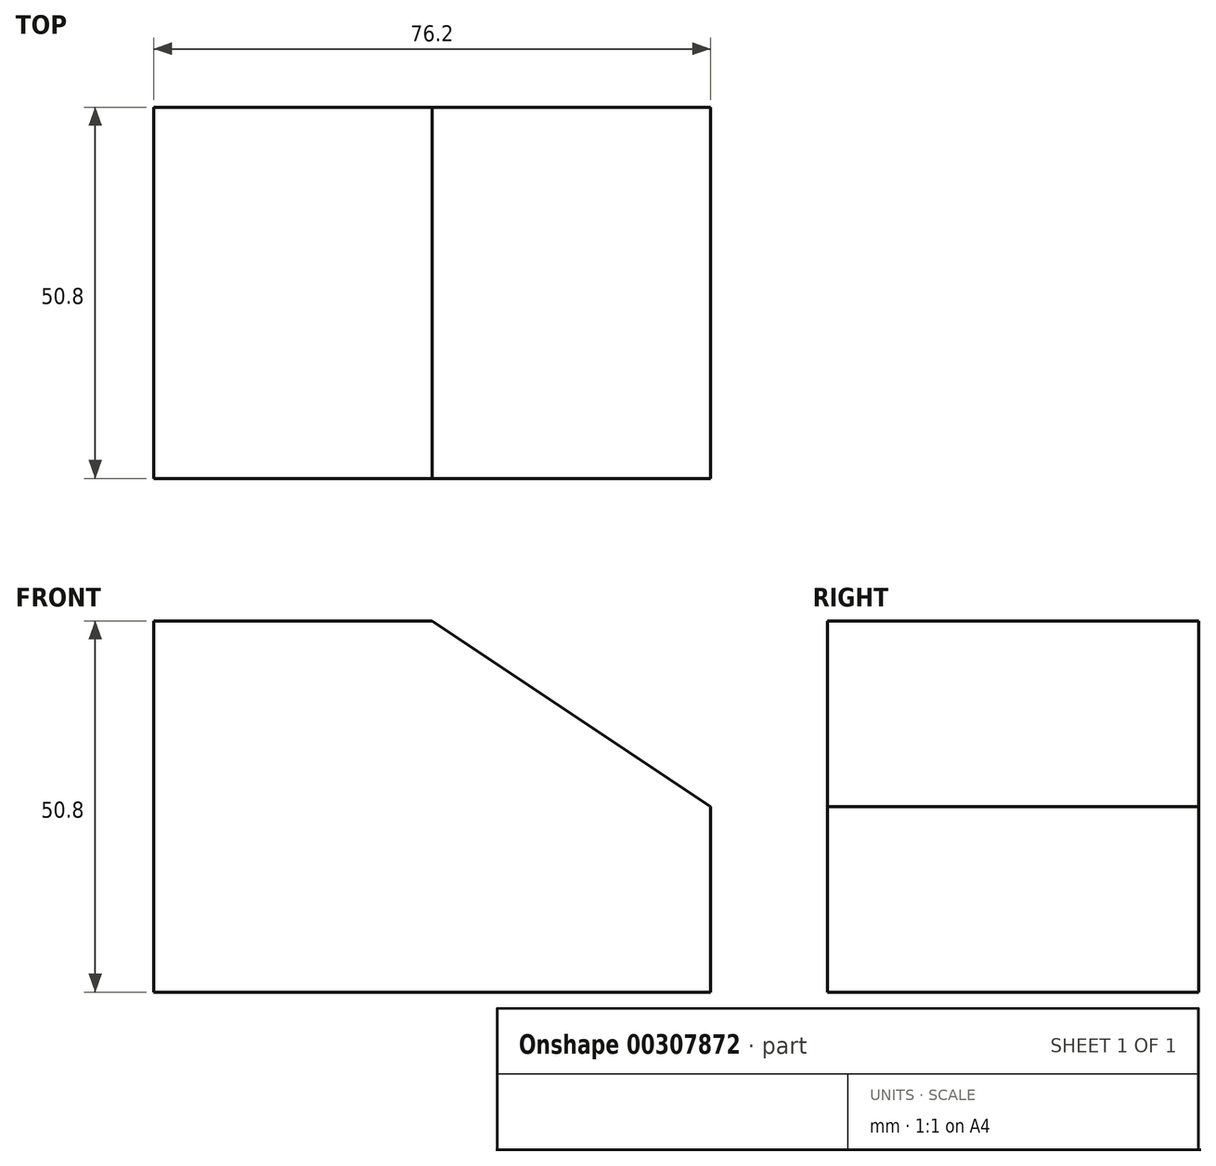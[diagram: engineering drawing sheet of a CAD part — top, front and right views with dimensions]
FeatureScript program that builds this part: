
annotation { "Feature Type Name" : "Feature", "Feature Type Description" : "" }
export const myFeature = defineFeature(function(context is Context, id is Id, definition is map)
    precondition{}
    {
        {
            var Q0;
            Q0=qCreatedBy(makeId("Front.planeOp"),FACE);
            var sketch = newSketch(context, id + "F0", { "sketchPlane" : qUnion([Q0])});
            skLineSegment(sketch, "E0", {"start": v(-61.5, 42.48) * mm, "end": v(-61.5, -8.32) * mm});
            skLineSegment(sketch, "E1", {"start": v(-61.5, -8.32) * mm, "end": v(14.7, -8.32) * mm});
            skLineSegment(sketch, "E2", {"start": v(14.7, -8.32) * mm, "end": v(14.7, 17.08) * mm});
            skLineSegment(sketch, "E3", {"start": v(-61.5, 42.48) * mm, "end": v(-23.4, 42.48) * mm});
            skLineSegment(sketch, "E4", {"start": v(14.7, 17.08) * mm, "end": v(-23.4, 42.48) * mm});
            skSolve(sketch);
        }
        {
            var Q0;
            Q0=makeQuery(id+"F0.imprint","IMPRINT",FACE,{"disambiguationData":[TD([[makeQuery(id+"F0.imprint","IMPRINT",EDGE,{"derivedFrom":sQuery(id+"F0.wireOp",EDGE,"E0")}),1.0]])]});
            extrude(context, id + "F1", {"entities" : qUnion([Q0]), "depth" : 50.8 * mm});
        }
    });
